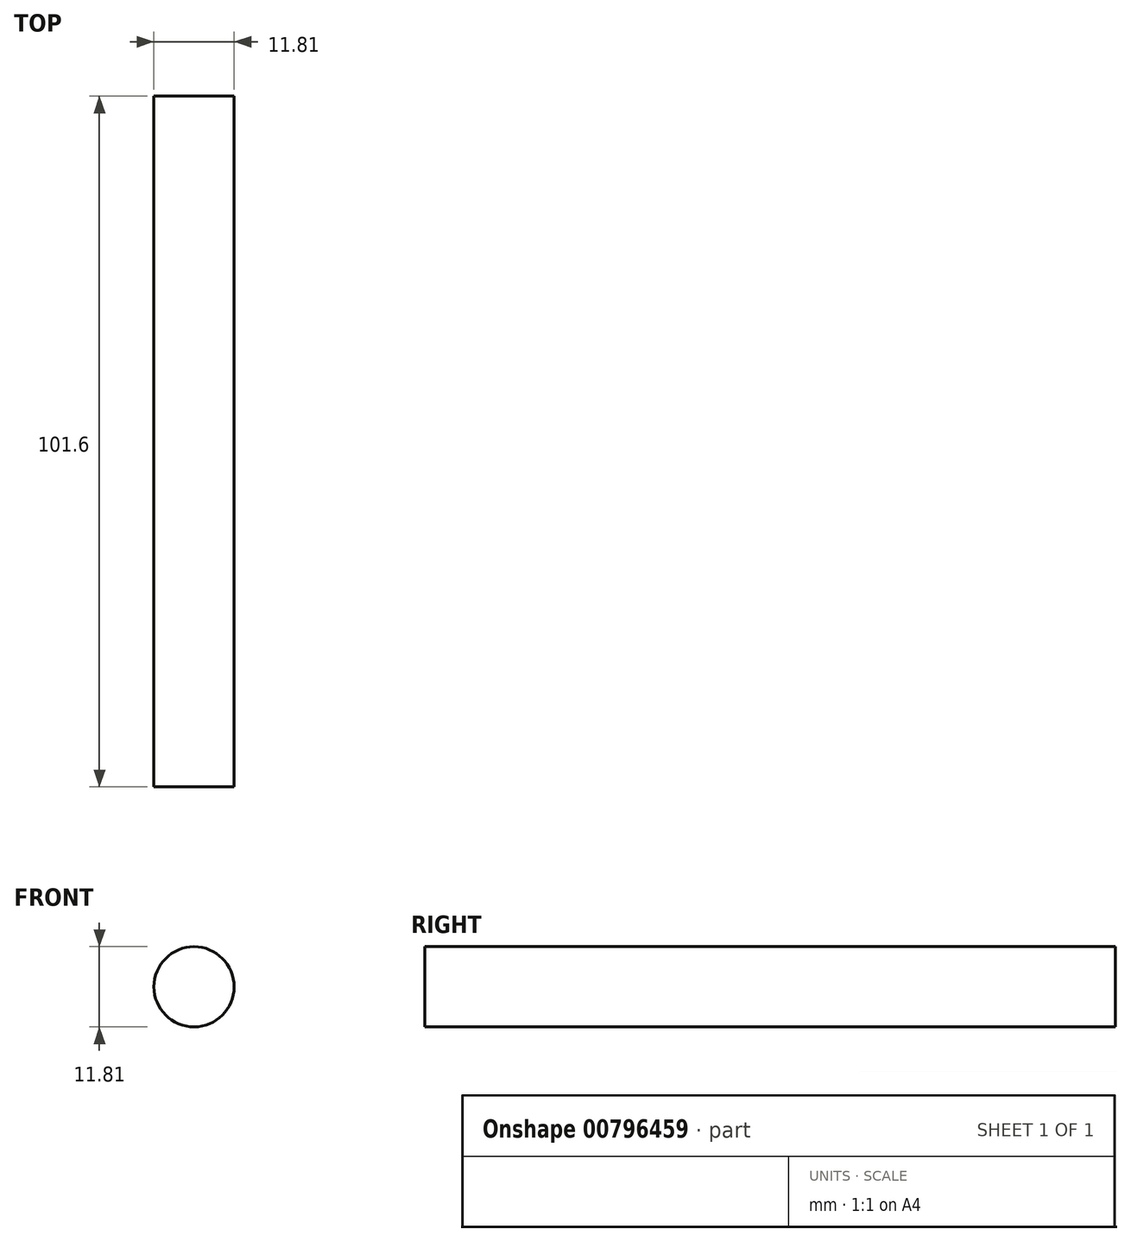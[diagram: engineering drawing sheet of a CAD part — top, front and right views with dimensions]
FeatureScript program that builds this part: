
annotation { "Feature Type Name" : "Feature", "Feature Type Description" : "" }
export const myFeature = defineFeature(function(context is Context, id is Id, definition is map)
    precondition{}
    {
        {
            var Q0;
            Q0=qCreatedBy(makeId("Right.planeOp"),FACE);
            var sketch = newSketch(context, id + "F0", { "sketchPlane" : qUnion([Q0])});
            skLineSegment(sketch, "E0.bottom", {"start": v(76.17, -20.99) * mm, "end": v(-76.17, -20.99) * mm});
            skLineSegment(sketch, "E0.top", {"start": v(76.17, 20.99) * mm, "end": v(-76.17, 20.99) * mm});
            skLineSegment(sketch, "E0.left", {"start": v(76.17, -20.99) * mm, "end": v(76.17, 20.99) * mm});
            skLineSegment(sketch, "E0.right", {"start": v(-76.17, -20.99) * mm, "end": v(-76.17, 20.99) * mm});
            skPoint(sketch, "E0.middle", {"position": v(0, 0) * mm});
            skSolve(sketch);
        }
        {
            var Q0;
            Q0=makeQuery(id+"F0.imprint","IMPRINT",FACE,{"disambiguationData":[TD([[makeQuery(id+"F0.imprint","IMPRINT",EDGE,{"derivedFrom":sQuery(id+"F0.wireOp",EDGE,"E0.bottom")}),-1.0]])]});
            extrude(context, id + "F1", {"entities" : qUnion([Q0]), "depth" : 69.85 * mm, "offsetDistance" : 25.4 * mm});
        }
        {
            var Q0;
            Q0=makeQuery(id+"F1.opExtrude","SWEPT_FACE",FACE,{"disambiguationData":[OSD([sQuery(id+"F0.wireOp",EDGE,"E0.top")])]});
            var sketch = newSketch(context, id + "F2", { "sketchPlane" : qUnion([Q0])});
            skCircle(sketch, "E1", {"center": v(36.18, -40.26) * mm, "radius": 22.58 * mm});
            skSolve(sketch);
        }
        {
            var Q0;
            Q0=makeQuery(id+"F2.imprint","IMPRINT",FACE,{"disambiguationData":[TD([[makeQuery(id+"F2.imprint","IMPRINT",EDGE,{"derivedFrom":sQuery(id+"F2.wireOp",EDGE,"E1")}),1.0]])]});
            extrude(context, id + "F3", {"entities" : qUnion([Q0]), "operationType" : NewBodyOperationType.ADD, "depth" : 25.4 * mm, "offsetDistance" : 25.4 * mm});
        }
        {
            var Q0;
            Q0=makeQuery(id+"F3.opExtrude","CAP_EDGE",EDGE,{"disambiguationData":[OSD([sQuery(id+"F2.wireOp",EDGE,"E1")])],"isStart":false});
            fillet(context, id + "F4", {"entities" : qUnion([Q0]), "radius" : 15.24 * mm, "tangentPropagation" : true, "allowEdgeOverflow" : false});
        }
        {
            var Q0;
            Q0=makeQuery(id+"F1.opExtrude","SWEPT_FACE",FACE,{"disambiguationData":[OSD([sQuery(id+"F0.wireOp",EDGE,"E0.top")])]});
            var sketch = newSketch(context, id + "F5", { "sketchPlane" : qUnion([Q0])});
            skLineSegment(sketch, "E2.bottom", {"start": v(14.94, -53.45) * mm, "end": v(0.74, -53.45) * mm});
            skLineSegment(sketch, "E2.top", {"start": v(14.94, -58.06) * mm, "end": v(0.74, -58.06) * mm});
            skLineSegment(sketch, "E2.left", {"start": v(14.94, -53.45) * mm, "end": v(14.94, -58.06) * mm});
            skLineSegment(sketch, "E2.right", {"start": v(0.74, -53.45) * mm, "end": v(0.74, -58.06) * mm});
            skPoint(sketch, "E2.middle", {"position": v(7.84, -55.75) * mm});
            skSolve(sketch);
        }
        {
            var Q0;
            Q0 = qSketchRegion(id + "F5", true);
            extrude(context, id + "F6", {"entities" : qUnion([Q0]), "operationType" : NewBodyOperationType.ADD, "depth" : 25.4 * mm, "offsetDistance" : 25.4 * mm});
        }
        {
            var Q0;
            Q0=makeQuery(id+"F6.opExtrude","SWEPT_FACE",FACE,{"disambiguationData":[OSD([sQuery(id+"F5.wireOp",EDGE,"E2.top")])]});
            var sketch = newSketch(context, id + "F7", { "sketchPlane" : qUnion([Q0])});
            skCircle(sketch, "E3", {"center": v(36.56, 31.04) * mm, "radius": 5.9 * mm});
            skSolve(sketch);
        }
        {
            var Q0;
            Q0=sQuery(id+"F7.wireOp",EDGE,"E3");
            extrude(context, id + "F8", {"bodyType" : ToolBodyType.SURFACE, "surfaceEntities" : qUnion([Q0]), "depth" : 101.6 * mm, "offsetDistance" : 25.4 * mm});
        }
        {
            var Q0;
            Q0=makeQuery(id+"F1.opExtrude","SWEPT_BODY",BODY,{"disambiguationData":[OSD([sQuery(id+"F0.wireOp",EDGE,"E0.bottom"),sQuery(id+"F0.wireOp",EDGE,"E0.top"),sQuery(id+"F0.wireOp",EDGE,"E0.left"),sQuery(id+"F0.wireOp",EDGE,"E0.right")])]});
            deleteBodies(context, id + "F9", {"entities" : qUnion([Q0])});
        }
    });
